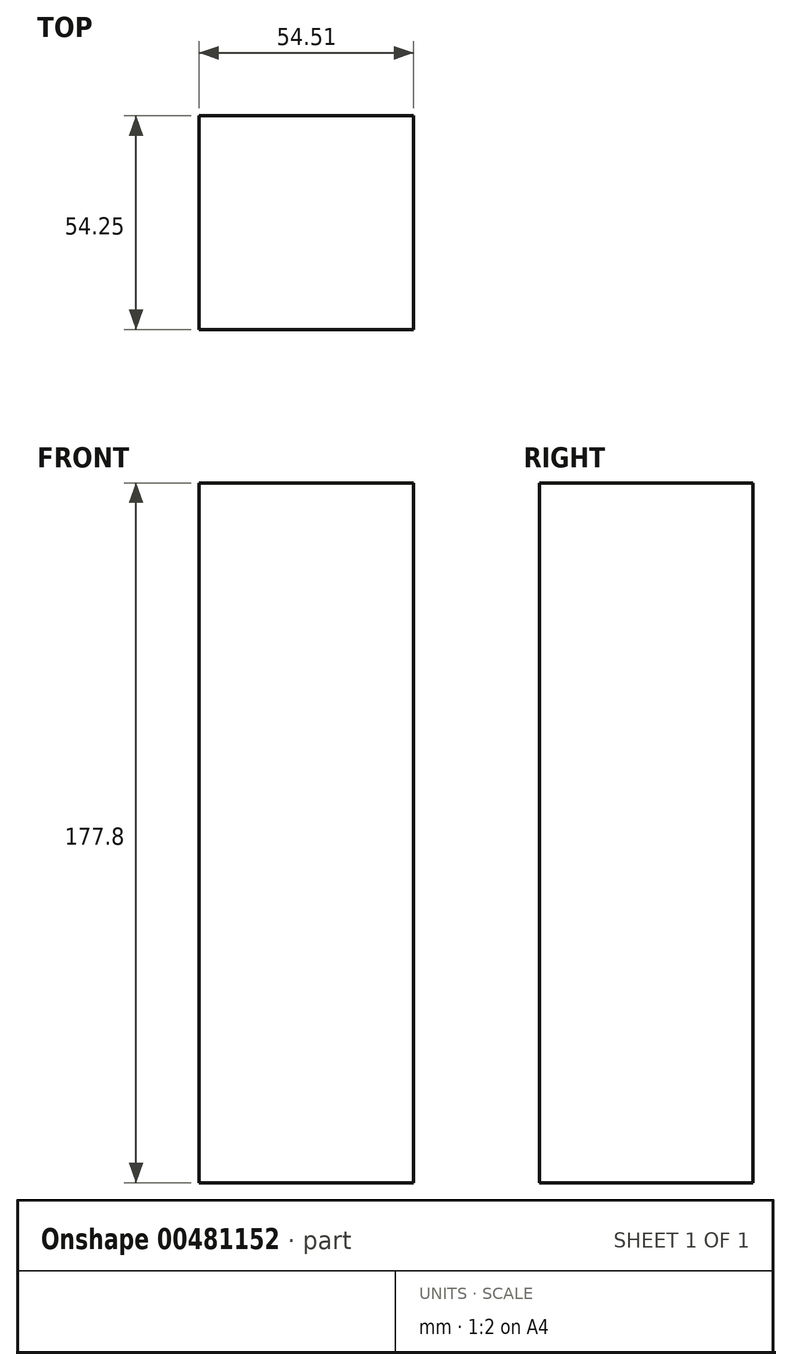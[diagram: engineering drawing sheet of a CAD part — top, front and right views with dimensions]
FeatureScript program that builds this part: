
annotation { "Feature Type Name" : "Feature", "Feature Type Description" : "" }
export const myFeature = defineFeature(function(context is Context, id is Id, definition is map)
    precondition{}
    {
        {
            var Q0;
            Q0=qCreatedBy(makeId("Top.planeOp"),FACE);
            var sketch = newSketch(context, id + "F0", { "sketchPlane" : qUnion([Q0])});
            skLineSegment(sketch, "E0.bottom", {"start": v(0.2, 2.5) * mm, "end": v(-54.3, 2.5) * mm});
            skLineSegment(sketch, "E0.top", {"start": v(0.2, 56.75) * mm, "end": v(-54.3, 56.75) * mm});
            skLineSegment(sketch, "E0.left", {"start": v(0.2, 2.5) * mm, "end": v(0.2, 56.75) * mm});
            skLineSegment(sketch, "E0.right", {"start": v(-54.3, 2.5) * mm, "end": v(-54.3, 56.75) * mm});
            skSolve(sketch);
        }
        {
            var Q0;
            Q0 = qSketchRegion(id + "F0", true);
            extrude(context, id + "F1", {"entities" : qUnion([Q0]), "depth" : 177.8 * mm});
        }
    });
